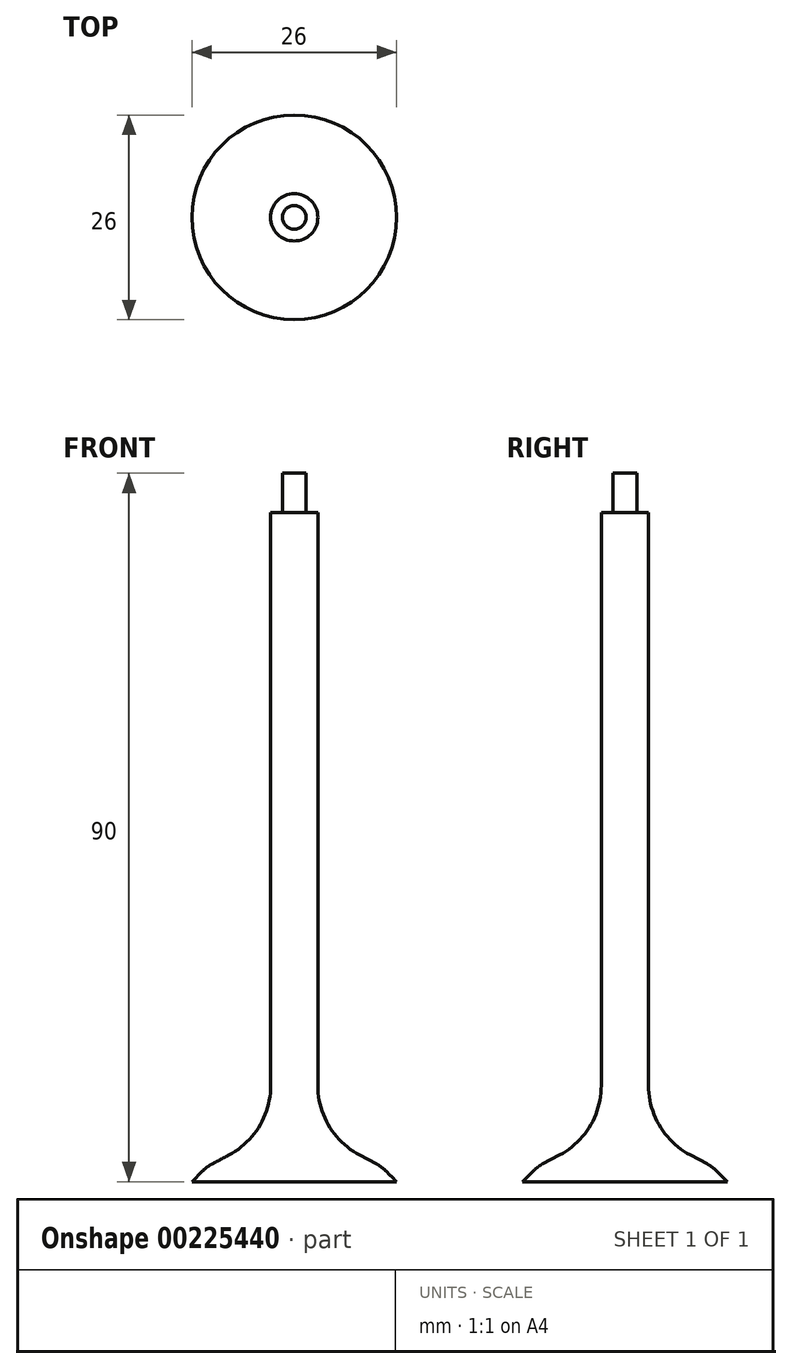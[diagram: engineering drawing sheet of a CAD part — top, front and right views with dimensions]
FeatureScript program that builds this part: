
annotation { "Feature Type Name" : "Feature", "Feature Type Description" : "" }
export const myFeature = defineFeature(function(context is Context, id is Id, definition is map)
    precondition{}
    {
        {
            var Q0;
            Q0=qCreatedBy(makeId("Front.planeOp"),FACE);
            var sketch = newSketch(context, id + "F0", { "sketchPlane" : qUnion([Q0])});
            skLineSegment(sketch, "E0", {"start": v(0, 0) * mm, "end": v(13, 0) * mm});
            skLineSegment(sketch, "E1", {"start": v(13, 0) * mm, "end": v(11.11, 1.89) * mm});
            skLineSegment(sketch, "E2", {"start": v(11.11, 1.89) * mm, "end": v(3, 6.2) * mm});
            skLineSegment(sketch, "E3", {"start": v(3, 6.2) * mm, "end": v(3, 85) * mm});
            skLineSegment(sketch, "E4", {"start": v(3, 85) * mm, "end": v(1.5, 85) * mm});
            skLineSegment(sketch, "E5", {"start": v(1.5, 85) * mm, "end": v(1.5, 90) * mm});
            skLineSegment(sketch, "E6", {"start": v(1.5, 90) * mm, "end": v(0, 90) * mm});
            skLineSegment(sketch, "E7", {"start": v(0, 90) * mm, "end": v(0, 0) * mm});
            skSolve(sketch);
        }
        {
            var Q0;
            Q0=qSketchRegion(id+"F0",true);
            var Q1;
            Q1=sQuery(id+"F0.wireOp",EDGE,"E7");
            revolve(context, id + "F1", {"entities" : qUnion([Q0]), "axis" : qUnion([Q1]), "revolveType" : RevolveType.FULL});
        }
        {
            var Q0;
            Q0=makeQuery(id+"F1.opRevolve","SWEPT_EDGE",EDGE,{"disambiguationData":[OSD([sQuery(id+"F0.wireOp",EDGE,"E2"),sQuery(id+"F0.wireOp",EDGE,"E3")])]});
            fillet(context, id + "F2", {"entities" : qUnion([Q0]), "radius" : 10 * mm, "tangentPropagation" : true, "allowEdgeOverflow" : false});
        }
        {
            var Q0;
            Q0=makeQuery(id+"F1.opRevolve","SWEPT_EDGE",EDGE,{"disambiguationData":[OSD([sQuery(id+"F0.wireOp",EDGE,"E1"),sQuery(id+"F0.wireOp",EDGE,"E2")])]});
            fillet(context, id + "F3", {"entities" : qUnion([Q0]), "radius" : 5 * mm, "tangentPropagation" : true, "allowEdgeOverflow" : false});
        }
    });
